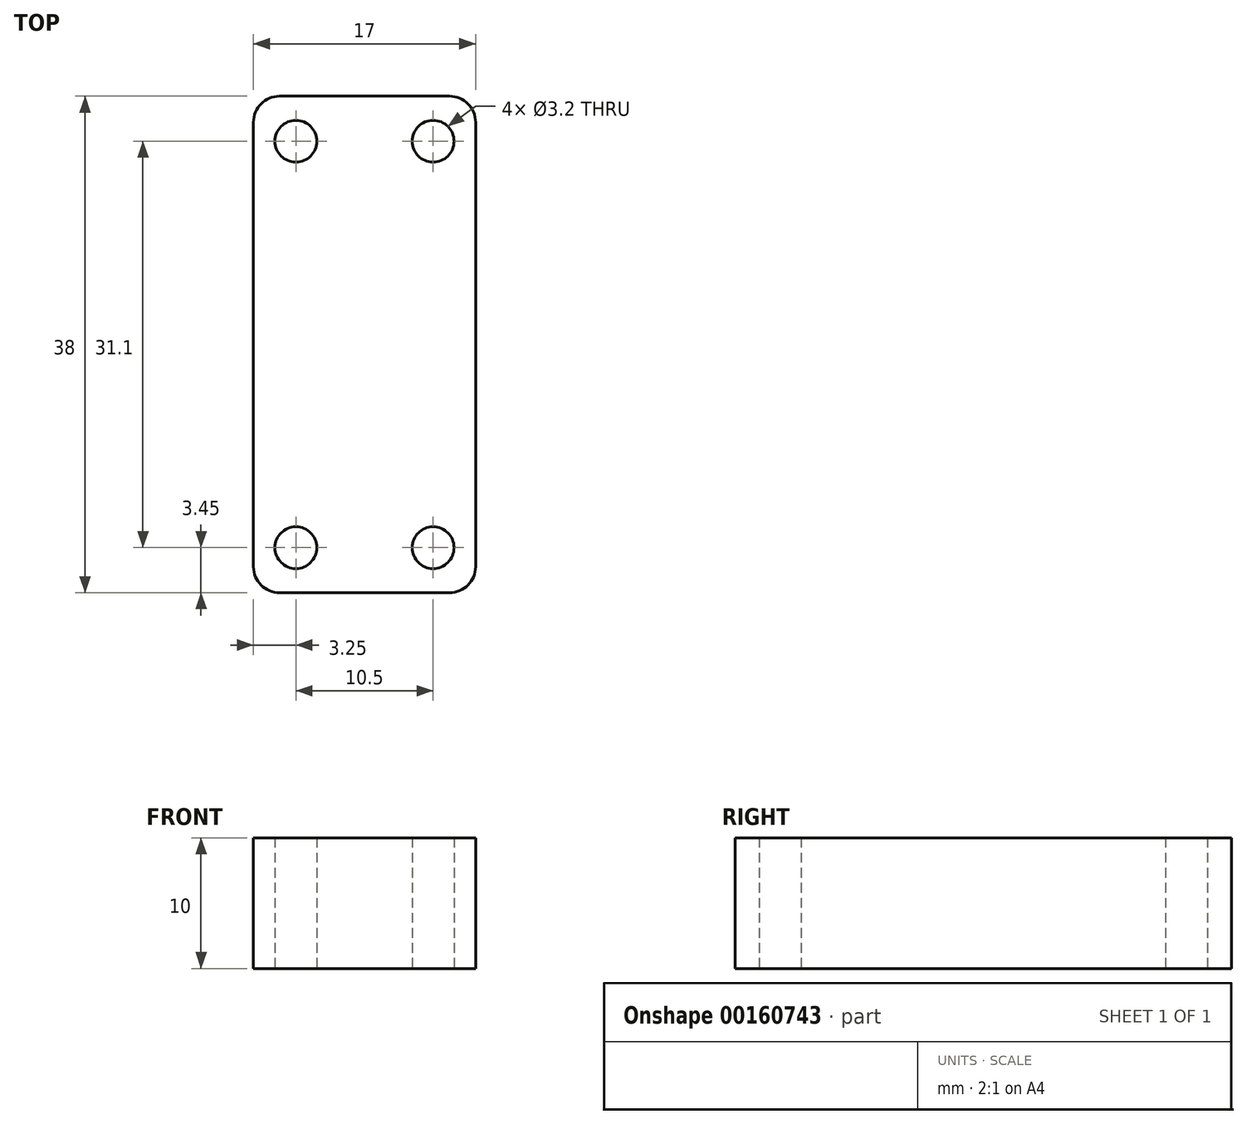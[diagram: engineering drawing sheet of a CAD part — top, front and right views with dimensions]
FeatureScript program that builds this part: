
annotation { "Feature Type Name" : "Feature", "Feature Type Description" : "" }
export const myFeature = defineFeature(function(context is Context, id is Id, definition is map)
    precondition{}
    {
        {
            var Q0;
            Q0=qCreatedBy(makeId("Top.planeOp"),FACE);
            var sketch = newSketch(context, id + "F0", { "sketchPlane" : qUnion([Q0])});
            skLineSegment(sketch, "E0.bottom", {"start": v(-8.5, 19) * mm, "end": v(8.5, 19) * mm});
            skLineSegment(sketch, "E0.top", {"start": v(-8.5, -19) * mm, "end": v(8.5, -19) * mm});
            skLineSegment(sketch, "E0.left", {"start": v(-8.5, 19) * mm, "end": v(-8.5, -19) * mm});
            skLineSegment(sketch, "E0.right", {"start": v(8.5, 19) * mm, "end": v(8.5, -19) * mm});
            skPoint(sketch, "E1", {"position": v(-8.5, 0) * mm});
            skPoint(sketch, "E2", {"position": v(0, 19) * mm});
            skLineSegment(sketch, "E3.bottom", {"start": v(-5.25, 15.55) * mm, "end": v(5.25, 15.55) * mm, "construction": true});
            skLineSegment(sketch, "E3.top", {"start": v(-5.25, -15.55) * mm, "end": v(5.25, -15.55) * mm, "construction": true});
            skLineSegment(sketch, "E3.left", {"start": v(-5.25, 15.55) * mm, "end": v(-5.25, -15.55) * mm, "construction": true});
            skLineSegment(sketch, "E3.right", {"start": v(5.25, 15.55) * mm, "end": v(5.25, -15.55) * mm, "construction": true});
            skPoint(sketch, "E4", {"position": v(0, 15.55) * mm});
            skPoint(sketch, "E5", {"position": v(-5.25, 0) * mm});
            skCircle(sketch, "E6", {"center": v(-5.25, 15.55) * mm, "radius": 1.6 * mm});
            skCircle(sketch, "E7", {"center": v(5.25, 15.55) * mm, "radius": 1.6 * mm});
            skCircle(sketch, "E8", {"center": v(5.25, -15.55) * mm, "radius": 1.6 * mm});
            skCircle(sketch, "E9", {"center": v(-5.25, -15.55) * mm, "radius": 1.6 * mm});
            skSolve(sketch);
        }
        {
            var Q0;
            Q0=makeQuery(id+"F0.imprint","IMPRINT",FACE,{"disambiguationData":[TD([[makeQuery(id+"F0.imprint","IMPRINT",EDGE,{"derivedFrom":sQuery(id+"F0.wireOp",EDGE,"E0.bottom")}),-1.0]])]});
            extrude(context, id + "F1", {"entities" : qUnion([Q0]), "depth" : 10 * mm});
        }
        {
            var Q0;
            Q0=makeQuery(id+"F1.opExtrude","SWEPT_EDGE",EDGE,{"disambiguationData":[OSD([sQuery(id+"F0.wireOp",EDGE,"E0.top"),sQuery(id+"F0.wireOp",EDGE,"E0.right")])]});
            var Q1;
            Q1=makeQuery(id+"F1.opExtrude","SWEPT_EDGE",EDGE,{"disambiguationData":[OSD([sQuery(id+"F0.wireOp",EDGE,"E0.top"),sQuery(id+"F0.wireOp",EDGE,"E0.left")])]});
            var Q2;
            Q2=makeQuery(id+"F1.opExtrude","SWEPT_EDGE",EDGE,{"disambiguationData":[OSD([sQuery(id+"F0.wireOp",EDGE,"E0.bottom"),sQuery(id+"F0.wireOp",EDGE,"E0.right")])]});
            var Q3;
            Q3=makeQuery(id+"F1.opExtrude","SWEPT_EDGE",EDGE,{"disambiguationData":[OSD([sQuery(id+"F0.wireOp",EDGE,"E0.bottom"),sQuery(id+"F0.wireOp",EDGE,"E0.left")])]});
            fillet(context, id + "F2", {"entities" : qUnion([Q0, Q1, Q2, Q3]), "radius" : 2 * mm, "tangentPropagation" : true, "allowEdgeOverflow" : false});
        }
    });
